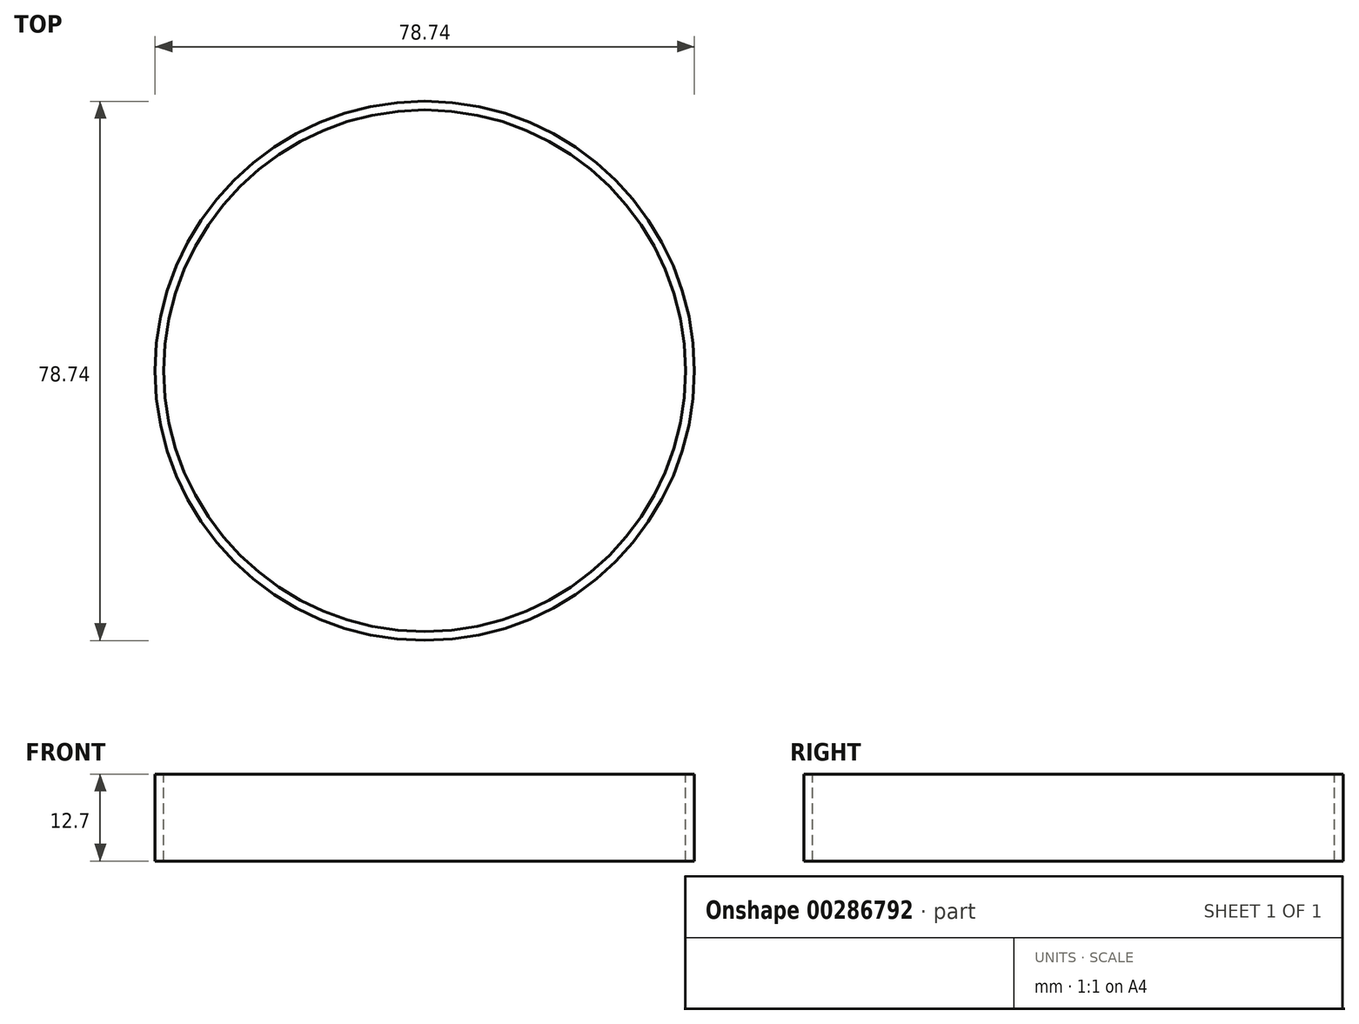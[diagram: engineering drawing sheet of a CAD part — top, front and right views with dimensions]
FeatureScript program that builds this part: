
annotation { "Feature Type Name" : "Feature", "Feature Type Description" : "" }
export const myFeature = defineFeature(function(context is Context, id is Id, definition is map)
    precondition{}
    {
        {
            var Q0;
            Q0=qCreatedBy(makeId("Top.planeOp"),FACE);
            var sketch = newSketch(context, id + "F0", { "sketchPlane" : qUnion([Q0])});
            skCircle(sketch, "E0", {"center": v(-7.2, 11.07) * mm, "radius": 38.1 * mm});
            skCircle(sketch, "E1.0", {"center": v(-7.2, 11.07) * mm, "radius": 39.37 * mm});
            skSolve(sketch);
        }
        {
            var Q0;
            Q0 = qConstructionFilter(qBodyType(qCreatedBy(id + "F0" ,EDGE), BodyType.WIRE), ConstructionObject.NO);
            extrude(context, id + "F1", {"bodyType" : ToolBodyType.SURFACE, "surfaceEntities" : qUnion([Q0]), "depth" : 12.7 * mm});
        }
    });
